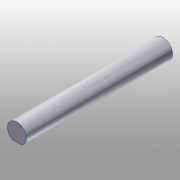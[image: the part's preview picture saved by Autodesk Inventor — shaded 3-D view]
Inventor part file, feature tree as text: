
AUTODESK INVENTOR PART (.ipt)
format: ipt  version: 2016 (Build 200138000, 138)  size: 88,576 bytes
history: native  units: mm
features: extrude x2, sketch x2
ambient origin geometry x8: Origin, YZ Plane, XZ Plane, XY Plane, X Axis, Y Axis, Z Axis, Center Point
bodies: Solid1 (feature_tree)
feature tree (4):
  extrude  "Extrusion1"  Depth=23.0mm TaperAngle=0.0deg
  extrude  "Extrusion2"  Depth=23.0mm TaperAngle=0.0deg
  sketch  "Sketch1"  dims[d0=3.0mm d1=23.0mm d2=0.0mm]
  sketch  "Sketch2"  dims[d3=1.3mm d4=23.0mm d5=0.0mm]
